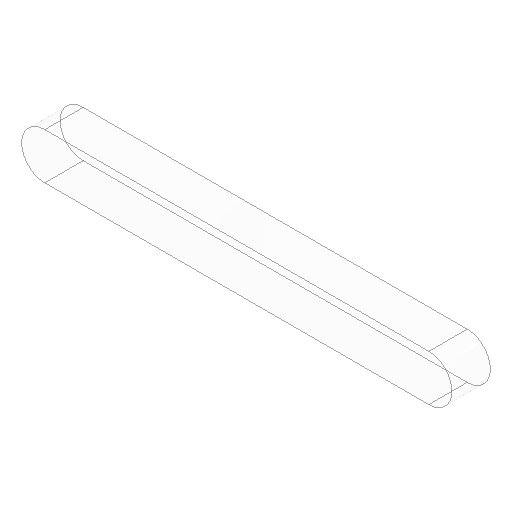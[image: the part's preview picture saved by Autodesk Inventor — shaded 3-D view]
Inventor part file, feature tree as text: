
AUTODESK INVENTOR PART (.ipt)
format: ipt  version: 2025.2 (Build 292293000, 293)  size: 85,504 bytes
history: native  units: mm
features: extrude x1, sketch x1
ambient origin geometry x8: Origin, YZ Plane, XZ Plane, XY Plane, X Axis, Y Axis, Z Axis, Center Point
bodies: Solid1 (feature_tree)
feature tree (2):
  extrude  "Extrusion1"  Depth=6.0mm
  sketch  "Sketch1"  dims[d0=50.0mm d1=6.0mm d2=5.0mm d3=0.0mm]
